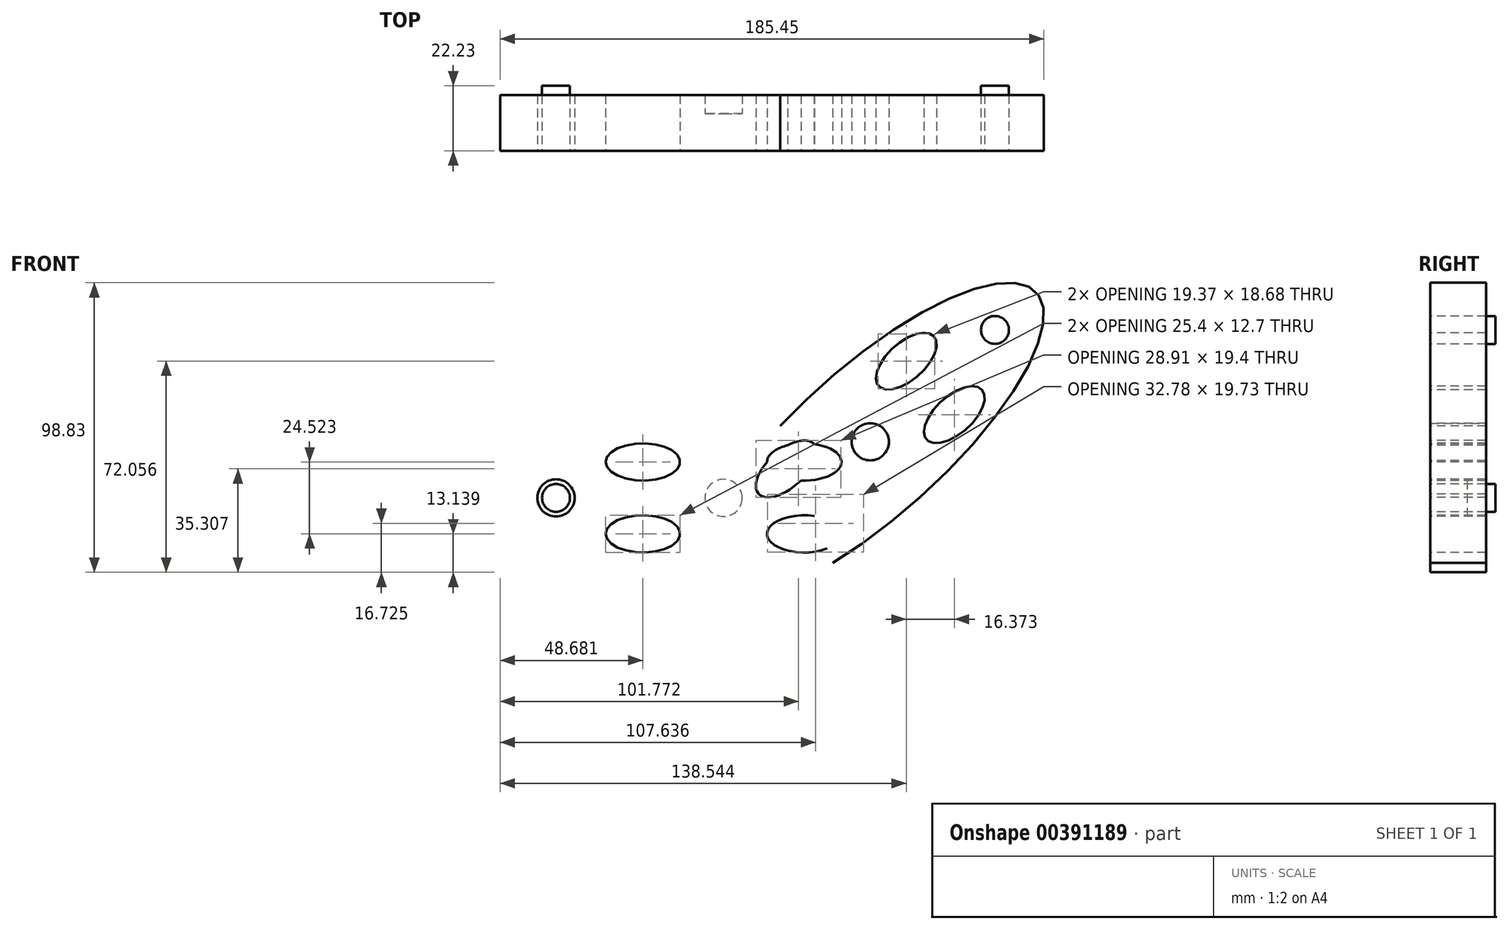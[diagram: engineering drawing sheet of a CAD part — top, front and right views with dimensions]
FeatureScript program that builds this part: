
annotation { "Feature Type Name" : "Feature", "Feature Type Description" : "" }
export const myFeature = defineFeature(function(context is Context, id is Id, definition is map)
    precondition{}
    {
        {
            var Q0;
            Q0=qCreatedBy(makeId("Front.planeOp"),FACE);
            var sketch = newSketch(context, id + "F0", { "sketchPlane" : qUnion([Q0])});
            skEllipticalArc(sketch, "E0", {});
            skCircle(sketch, "E1", {"center": v(0, 0) * mm, "radius": 6.35 * mm});
            skCircle(sketch, "E2", {"center": v(92.59, 57.31) * mm, "radius": 6.35 * mm});
            skLineSegment(sketch, "E3", {"start": v(0, 25.4) * mm, "end": v(0, -25.4) * mm, "construction": true});
            skCircle(sketch, "E4.MirrorC", {"center": v(-57.15, 0) * mm, "radius": 6.35 * mm});
            skLineSegment(sketch, "E5", {"start": v(-76.2, 0) * mm, "end": v(66.73, 0) * mm, "construction": true});
            skLineSegment(sketch, "E6.MirrorCS", {"start": v(-76.2, 0) * mm, "end": v(76.2, 0) * mm, "construction": true});
            skLineSegment(sketch, "E7.MirrorCS", {"start": v(-73.84, 0) * mm, "end": v(78.56, 0) * mm, "construction": true});
            skEllipse(sketch, "E8.MirrorC", {"center": v(-27.52, 12.26) * mm, "majorRadius": 12.7 * mm, "minorRadius": 6.35 * mm, "majorAxis": v(-1, 0)});
            skEllipticalArc(sketch, "E9.MirrorC", {});
            skLineSegment(sketch, "E10", {"start": v(0.37, -25.4) * mm, "end": v(106.77, 70.03) * mm, "construction": true});
            skLineSegment(sketch, "E11", {"start": v(50.04, 19.15) * mm, "end": v(67, 0.25) * mm, "construction": true});
            skLineSegment(sketch, "E12", {"start": v(50.04, 19.15) * mm, "end": v(33.09, 38.06) * mm, "construction": true});
            skPoint(sketch, "E13.orphan", {"position": v(-6.68, -31.72) * mm});
            skPoint(sketch, "E14.orphan", {"position": v(76.2, 0) * mm});
            skLineSegment(sketch, "E15", {"start": v(19.28, 24.57) * mm, "end": v(37.17, -22.17) * mm, "construction": true});
            skEllipse(sketch, "E16.MirrorC", {"center": v(62.34, 46.66) * mm, "majorRadius": 12.7 * mm, "minorRadius": 6.35 * mm, "majorAxis": v(0.74, 0.67)});
            skEllipse(sketch, "E17.MirrorC", {"center": v(-27.52, -12.26) * mm, "majorRadius": 12.7 * mm, "minorRadius": 6.35 * mm, "majorAxis": v(-1, 0)});
            skEllipse(sketch, "E18.MirrorC", {"center": v(78.72, 28.4) * mm, "majorRadius": 12.7 * mm, "minorRadius": 6.35 * mm, "majorAxis": v(0.74, 0.67)});
            skEllipticalArc(sketch, "E19.MirrorC", {});
            skEllipticalArc(sketch, "E20.MirrorC", {});
            skEllipticalArc(sketch, "E21.MirrorC", {});
            skEllipticalArc(sketch, "E22.MirrorC", {});
            skEllipticalArc(sketch, "E23.trimOffspring", {});
            skEllipticalArc(sketch, "E24.trimOffspring", {});
            skCircle(sketch, "E25.MirrorC", {"center": v(50.04, 19.15) * mm, "radius": 6.35 * mm});
            skCircle(sketch, "E26", {"center": v(92.59, 57.31) * mm, "radius": 4.76 * mm});
            skCircle(sketch, "E27", {"center": v(-57.15, 0) * mm, "radius": 4.76 * mm});
            const initialGuessF0  = {"E0": [0, 0, 1, 0, 0.0762, 0.0254, 1.314963761471085, 5.222014936703207], "E9.MirrorC": [0.05004441194956987, 0.019154334678029728, -0.7444471243751429, -0.6676814202968213, 0.0762, 0.0254, 1.0611703704763775, 4.968221545708502], "E19.MirrorC": [0.02751898020505905, 0.012261383542418482, 1, 0, 0.0127, 0.00635, 4.625437770756568, 1.307752789989924], "E20.MirrorC": [0.027518980205059038, -0.012261383542418505, 1, 0, 0.0127, 0.00635, 1.2893779228761877, 5.371981629429969], "E21.MirrorC": [0.021371288291771165, 0.00990837460860998, -0.7444471243751428, -0.6676814202968214, 0.0127, 0.00635, 3.142658646833828, 4.247263525630003], "E22.MirrorC": [0.03774468424858328, -0.008347528829418305, -0.7444471243751425, -0.667681420296822, 0.0127, 0.00635, 0.9112036777495996, 4.993807384303406], "E23.trimOffspring": [0.02751898020505905, 0.012261383542418482, 1, 0, 0.0127, 0.00635, 2.0359217815495914, 3.1405266603457442], "E24.trimOffspring": [0.021371288291771165, 0.00990837460860998, -0.7444471243751428, -0.6676814202968214, 0.0127, 0.00635, 4.97543251718966, 1.657747536423008]};
            skSetInitialGuess(sketch, initialGuessF0);
            skSolve(sketch);
        }
        {
            var Q0;
            Q0=makeQuery(id+"F0.imprint","IMPRINT",FACE,{"disambiguationData":[TD([[makeQuery(id+"F0.imprint","IMPRINT",EDGE,{"derivedFrom":sQuery(id+"F0.wireOp",EDGE,"E0")}),1.0]])]});
            extrude(context, id + "F1", {"entities" : qUnion([Q0]), "oppositeDirection" : true, "depth" : 6.35 * mm});
        }
        {
            var Q0;
            Q0=makeQuery(id+"F0.imprint","IMPRINT",FACE,{"disambiguationData":[TD([[makeQuery(id+"F0.imprint","IMPRINT",EDGE,{"derivedFrom":sQuery(id+"F0.wireOp",EDGE,"E4.MirrorC")}),-1.0]])]});
            extrude(context, id + "F2", {"entities" : qUnion([Q0]), "operationType" : NewBodyOperationType.ADD, "oppositeDirection" : true, "depth" : 19.05 * mm});
        }
        {
            var Q0;
            Q0=makeQuery(id+"F0.imprint","IMPRINT",FACE,{"disambiguationData":[TD([[makeQuery(id+"F0.imprint","IMPRINT",EDGE,{"derivedFrom":sQuery(id+"F0.wireOp",EDGE,"E2")}),1.0]])]});
            extrude(context, id + "F3", {"entities" : qUnion([Q0]), "operationType" : NewBodyOperationType.ADD, "oppositeDirection" : true, "depth" : 19.05 * mm});
        }
        {
            var Q0;
            Q0=makeQuery(id+"F0.imprint","IMPRINT",FACE,{"disambiguationData":[TD([[makeQuery(id+"F0.imprint","IMPRINT",EDGE,{"derivedFrom":sQuery(id+"F0.wireOp",EDGE,"E1")}),1.0]])]});
            extrude(context, id + "F4", {"entities" : qUnion([Q0]), "operationType" : NewBodyOperationType.ADD, "oppositeDirection" : true, "depth" : 12.7 * mm});
        }
        {
            var Q0;
            Q0=makeQuery(id+"F0.imprint","IMPRINT",FACE,{"disambiguationData":[TD([[makeQuery(id+"F0.imprint","IMPRINT",EDGE,{"derivedFrom":sQuery(id+"F0.wireOp",EDGE,"E25.MirrorC")}),-1.0]])]});
            extrude(context, id + "F5", {"entities" : qUnion([Q0]), "operationType" : NewBodyOperationType.ADD, "oppositeDirection" : true, "depth" : 12.7 * mm});
        }
        {
            var Q0;
            Q0=makeQuery(id+"F0.imprint","IMPRINT",FACE,{"disambiguationData":[TD([[makeQuery(id+"F0.imprint","IMPRINT",EDGE,{"derivedFrom":sQuery(id+"F0.wireOp",EDGE,"E26")}),1.0]])]});
            extrude(context, id + "F6", {"entities" : qUnion([Q0]), "oppositeDirection" : true, "depth" : 22.22 * mm});
        }
        {
            var Q0;
            Q0=makeQuery(id+"F0.imprint","IMPRINT",FACE,{"disambiguationData":[TD([[makeQuery(id+"F0.imprint","IMPRINT",EDGE,{"derivedFrom":sQuery(id+"F0.wireOp",EDGE,"E27")}),1.0]])]});
            extrude(context, id + "F7", {"entities" : qUnion([Q0]), "operationType" : NewBodyOperationType.ADD, "oppositeDirection" : true, "depth" : 22.22 * mm});
        }
    });
